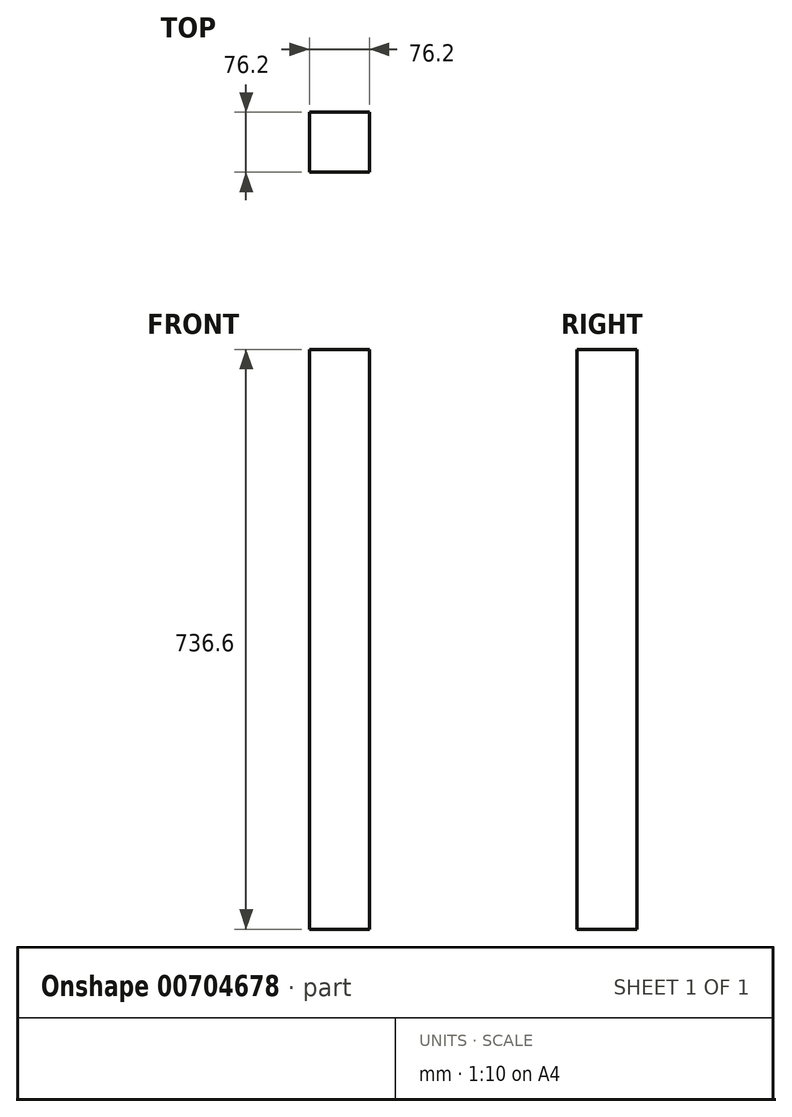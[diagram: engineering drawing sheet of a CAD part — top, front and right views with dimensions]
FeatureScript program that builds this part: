
annotation { "Feature Type Name" : "Feature", "Feature Type Description" : "" }
export const myFeature = defineFeature(function(context is Context, id is Id, definition is map)
    precondition{}
    {
        {
            var Q0;
            Q0=qCreatedBy(makeId("Top.planeOp"),FACE);
            var sketch = newSketch(context, id + "F0", { "sketchPlane" : qUnion([Q0])});
            skLineSegment(sketch, "E0.bottom", {"start": v(112.36, -76.2) * mm, "end": v(188.56, -76.2) * mm});
            skLineSegment(sketch, "E0.top", {"start": v(112.36, 0) * mm, "end": v(188.56, 0) * mm});
            skLineSegment(sketch, "E0.left", {"start": v(112.36, -76.2) * mm, "end": v(112.36, 0) * mm});
            skLineSegment(sketch, "E0.right", {"start": v(188.56, -76.2) * mm, "end": v(188.56, 0) * mm});
            skSolve(sketch);
        }
        {
            var Q0;
            Q0 = qSketchRegion(id + "F0", true);
            extrude(context, id + "F1", {"entities" : qUnion([Q0]), "depth" : 736.6 * mm, "offsetDistance" : 25.4 * mm});
        }
    });
